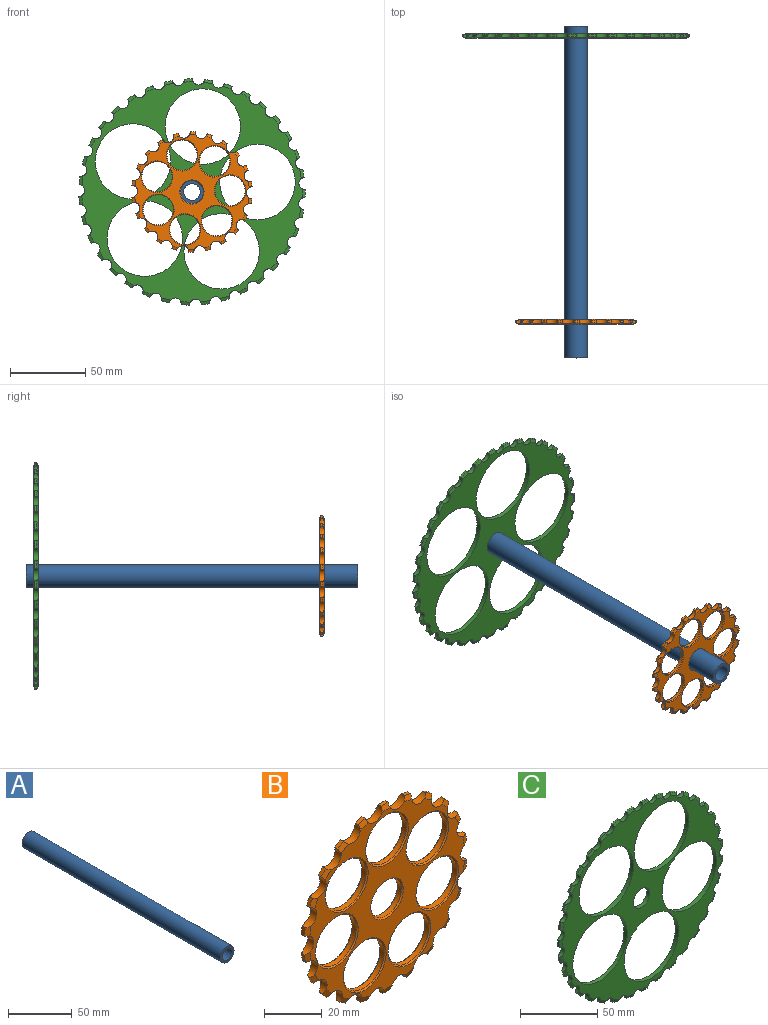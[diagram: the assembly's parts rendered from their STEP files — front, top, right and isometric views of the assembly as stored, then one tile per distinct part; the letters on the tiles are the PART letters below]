
ASSEMBLY  parts=3 mates=2
PART A: 4 faces, bbox 15x220x15 mm
  f0: cylinder r=5.5mm len=220mm, axis (0,1,0), area 7602.7mm2, adj f2,f3
  f1: cylinder r=7.5mm len=220mm, axis (0,1,0), area 10367.3mm2, adj f2,f3
  f2: plane 15x15mm, normal (0,-1,0), area 81.7mm2, adj f0,f1
  f3: plane 15x15mm, normal (0,1,0), area 81.7mm2, adj f0,f1
PART B: 114 faces, bbox 79.8x3x80 mm
  f0: cylinder r=4mm len=7.28mm, axis (0,1,0), area 33.4mm2, adj f1,f50,f52,f53,f61,f62,f83,f84
  f1: cylinder r=40mm len=3.13mm, axis (0,1,0), area 5.1mm2, adj f0,f2,f61,f83
  f2: cylinder r=4mm len=7.79mm, axis (0,1,0), area 33.4mm2, adj f1,f3,f52,f53,f60,f61,f82,f83
  f3: cylinder r=40mm len=3.39mm, axis (0,1,0), area 5.1mm2, adj f2,f4,f60,f82
  f4: cylinder r=4mm len=7.99mm, axis (0,1,0), area 33.4mm2, adj f3,f5,f52,f53,f59,f60,f81,f82
  f5: cylinder r=40mm len=3.38mm, axis (0,1,0), area 5.1mm2, adj f4,f6,f59,f81
  f6: cylinder r=4mm len=7.76mm, axis (0,1,0), area 33.4mm2, adj f5,f7,f52,f53,f58,f59,f80,f81
  f7: cylinder r=40mm len=3.09mm, axis (0,1,0), area 5.1mm2, adj f6,f8,f58,f80
  f8: cylinder r=4mm len=7.23mm, axis (0,1,0), area 33.4mm2, adj f7,f9,f52,f53,f57,f58,f79,f80
  f9: cylinder r=40mm len=2.56mm, axis (0,1,0), area 5.1mm2, adj f8,f10,f57,f79
  f10: cylinder r=4mm len=6.92mm, axis (0,1,0), area 33.4mm2, adj f9,f11,f52,f53,f56,f57,f78,f79
  f11: cylinder r=40mm len=2.9mm, axis (0,1,0), area 5.1mm2, adj f10,f12,f56,f78
  f12: cylinder r=4mm len=7.57mm, axis (0,1,0), area 33.4mm2, adj f11,f13,f52,f53,f55,f56,f77,f78
  f13: cylinder r=40mm len=3.29mm, axis (0,1,0), area 5.1mm2, adj f12,f14,f55,f77
  f14: cylinder r=4mm len=7.93mm, axis (0,1,0), area 33.4mm2, adj f13,f15,f52,f53,f54,f55,f76,f77
  f15: cylinder r=40mm len=3.42mm, axis (0,1,0), area 5.1mm2, adj f14,f16,f54,f76
  f16: cylinder r=4mm len=7.92mm, axis (0,1,0), area 33.4mm2, adj f15,f17,f52,f53,f54,f75,f76,f97
  f17: cylinder r=40mm len=3.27mm, axis (0,1,0), area 5.1mm2, adj f16,f18,f75,f97
  f18: cylinder r=4mm len=7.53mm, axis (0,1,0), area 33.4mm2, adj f17,f19,f52,f53,f74,f75,f96,f97
  f19: cylinder r=40mm len=2.86mm, axis (0,1,0), area 5.1mm2, adj f18,f20,f74,f96
  f20: cylinder r=4mm len=6.86mm, axis (0,1,0), area 33.4mm2, adj f19,f21,f52,f53,f73,f74,f95,f96
  f21: cylinder r=40mm len=2.61mm, axis (0,1,0), area 5.1mm2, adj f20,f22,f73,f95
  f22: cylinder r=4mm len=7.28mm, axis (0,1,0), area 33.4mm2, adj f21,f23,f52,f53,f72,f73,f94,f95
  f23: cylinder r=40mm len=3.13mm, axis (0,1,0), area 5.1mm2, adj f22,f24,f72,f94
  f24: cylinder r=4mm len=7.79mm, axis (0,1,0), area 33.4mm2, adj f23,f25,f52,f53,f71,f72,f93,f94
  f25: cylinder r=40mm len=3.39mm, axis (0,1,0), area 5.1mm2, adj f24,f26,f71,f93
  f26: cylinder r=4mm len=7.99mm, axis (0,1,0), area 33.4mm2, adj f25,f27,f52,f53,f70,f71,f92,f93
  f27: cylinder r=40mm len=3.38mm, axis (0,1,0), area 5.1mm2, adj f26,f28,f70,f92
  f28: cylinder r=4mm len=7.76mm, axis (0,1,0), area 33.4mm2, adj f27,f29,f52,f53,f69,f70,f91,f92
  f29: cylinder r=40mm len=3.09mm, axis (0,1,0), area 5.1mm2, adj f28,f30,f69,f91
  f30: cylinder r=4mm len=7.23mm, axis (0,1,0), area 33.4mm2, adj f29,f31,f52,f53,f68,f69,f90,f91
  f31: cylinder r=40mm len=2.56mm, axis (0,1,0), area 5.1mm2, adj f30,f32,f68,f90
  f32: cylinder r=4mm len=6.92mm, axis (0,1,0), area 33.4mm2, adj f31,f33,f52,f53,f67,f68,f89,f90
  f33: cylinder r=40mm len=2.9mm, axis (0,1,0), area 5.1mm2, adj f32,f34,f67,f89
  f34: cylinder r=4mm len=7.57mm, axis (0,1,0), area 33.4mm2, adj f33,f35,f52,f53,f66,f67,f88,f89
  f35: cylinder r=40mm len=3.29mm, axis (0,1,0), area 5.1mm2, adj f34,f36,f66,f88
  f36: cylinder r=4mm len=7.93mm, axis (0,1,0), area 33.4mm2, adj f35,f37,f52,f53,f65,f66,f87,f88
  f37: cylinder r=40mm len=3.42mm, axis (0,1,0), area 5.1mm2, adj f36,f38,f65,f87
  f38: cylinder r=4mm len=7.92mm, axis (0,1,0), area 33.4mm2, adj f37,f39,f52,f53,f64,f65,f86,f87
  f39: cylinder r=40mm len=3.27mm, axis (0,1,0), area 5.1mm2, adj f38,f40,f64,f86
  f40: cylinder r=4mm len=7.53mm, axis (0,1,0), area 33.4mm2, adj f39,f41,f52,f53,f63,f64,f85,f86
  f41: cylinder r=40mm len=2.86mm, axis (0,1,0), area 5.1mm2, adj f40,f42,f63,f85
  f42: cylinder r=4mm len=6.86mm, axis (0,1,0), area 33.4mm2, adj f41,f50,f52,f53,f62,f63,f84,f85
  f43: cylinder r=10mm len=20mm, axis (0,1,0), area 125.7mm2, adj f98,f105
  f44: cylinder r=10mm len=20mm, axis (0,1,0), area 125.7mm2, adj f99,f106
  f45: cylinder r=10mm len=20mm, axis (0,1,0), area 125.7mm2, adj f100,f107
  f46: cylinder r=10mm len=20mm, axis (0,1,0), area 125.7mm2, adj f101,f108
  f47: cylinder r=10mm len=20mm, axis (0,1,0), area 125.7mm2, adj f102,f109
  f48: cylinder r=10mm len=20mm, axis (0,1,0), area 125.7mm2, adj f103,f110
  f49: cylinder r=7.5mm len=15mm, axis (0,1,0), area 94.2mm2, adj f112,f113
  f50: cylinder r=40mm len=2.61mm, axis (0,1,0), area 5.1mm2, adj f0,f42,f62,f84
  f51: cylinder r=10mm len=20mm, axis (0,1,0), area 125.7mm2, adj f104,f111
  f52: plane 76x75.77mm, normal (0,-1,0), area 1702.4mm2, adj f0,f2,f4,f6,f8,f10,f12,f14
  f53: plane 76x75.77mm, normal (0,1,0), area 1702.4mm2, adj f0,f2,f4,f6,f8,f10,f12,f14
  f54: cone r=38mm half-angle=69.4deg, axis (0,1,0), area 7.6mm2, adj f14,f15,f16,f52
  f55: cone r=38mm half-angle=69.4deg, axis (0,1,0), area 7.6mm2, adj f12,f13,f14,f52
  f56: cone r=38mm half-angle=69.4deg, axis (0,1,0), area 7.6mm2, adj f10,f11,f12,f52
  f57: cone r=38mm half-angle=69.4deg, axis (0,1,0), area 7.6mm2, adj f8,f9,f10,f52
  f58: cone r=38mm half-angle=69.4deg, axis (0,1,0), area 7.6mm2, adj f6,f7,f8,f52
  f59: cone r=38mm half-angle=69.4deg, axis (0,1,0), area 7.6mm2, adj f4,f5,f6,f52
  f60: cone r=38mm half-angle=69.4deg, axis (0,1,0), area 7.6mm2, adj f2,f3,f4,f52
  f61: cone r=38mm half-angle=69.4deg, axis (0,1,0), area 7.6mm2, adj f0,f1,f2,f52
  f62: cone r=38mm half-angle=69.4deg, axis (0,1,0), area 7.6mm2, adj f0,f42,f50,f52
  f63: cone r=38mm half-angle=69.4deg, axis (0,1,0), area 7.6mm2, adj f40,f41,f42,f52
  f64: cone r=38mm half-angle=69.4deg, axis (0,1,0), area 7.6mm2, adj f38,f39,f40,f52
  f65: cone r=38mm half-angle=69.4deg, axis (0,1,0), area 7.6mm2, adj f36,f37,f38,f52
  f66: cone r=38mm half-angle=69.4deg, axis (0,1,0), area 7.6mm2, adj f34,f35,f36,f52
  f67: cone r=38mm half-angle=69.4deg, axis (0,1,0), area 7.6mm2, adj f32,f33,f34,f52
  f68: cone r=38mm half-angle=69.4deg, axis (0,1,0), area 7.6mm2, adj f30,f31,f32,f52
  f69: cone r=38mm half-angle=69.4deg, axis (0,1,0), area 7.6mm2, adj f28,f29,f30,f52
  f70: cone r=38mm half-angle=69.4deg, axis (0,1,0), area 7.6mm2, adj f26,f27,f28,f52
  f71: cone r=38mm half-angle=69.4deg, axis (0,1,0), area 7.6mm2, adj f24,f25,f26,f52
  f72: cone r=38mm half-angle=69.4deg, axis (0,1,0), area 7.6mm2, adj f22,f23,f24,f52
  f73: cone r=38mm half-angle=69.4deg, axis (0,1,0), area 7.6mm2, adj f20,f21,f22,f52
  f74: cone r=38mm half-angle=69.4deg, axis (0,1,0), area 7.6mm2, adj f18,f19,f20,f52
  f75: cone r=38mm half-angle=69.4deg, axis (0,1,0), area 7.6mm2, adj f16,f17,f18,f52
  f76: cone r=40mm half-angle=69.4deg, axis (0,-1,0), area 7.6mm2, adj f14,f15,f16,f53
  f77: cone r=40mm half-angle=69.4deg, axis (0,-1,0), area 7.6mm2, adj f12,f13,f14,f53
  f78: cone r=40mm half-angle=69.4deg, axis (0,-1,0), area 7.6mm2, adj f10,f11,f12,f53
  f79: cone r=40mm half-angle=69.4deg, axis (0,-1,0), area 7.6mm2, adj f8,f9,f10,f53
  f80: cone r=40mm half-angle=69.4deg, axis (0,-1,0), area 7.6mm2, adj f6,f7,f8,f53
  f81: cone r=40mm half-angle=69.4deg, axis (0,-1,0), area 7.6mm2, adj f4,f5,f6,f53
  f82: cone r=40mm half-angle=69.4deg, axis (0,-1,0), area 7.6mm2, adj f2,f3,f4,f53
  f83: cone r=40mm half-angle=69.4deg, axis (0,-1,0), area 7.6mm2, adj f0,f1,f2,f53
  f84: cone r=40mm half-angle=69.4deg, axis (0,-1,0), area 7.6mm2, adj f0,f42,f50,f53
  f85: cone r=40mm half-angle=69.4deg, axis (0,-1,0), area 7.6mm2, adj f40,f41,f42,f53
  f86: cone r=40mm half-angle=69.4deg, axis (0,-1,0), area 7.6mm2, adj f38,f39,f40,f53
  f87: cone r=40mm half-angle=69.4deg, axis (0,-1,0), area 7.6mm2, adj f36,f37,f38,f53
  f88: cone r=40mm half-angle=69.4deg, axis (0,-1,0), area 7.6mm2, adj f34,f35,f36,f53
  f89: cone r=40mm half-angle=69.4deg, axis (0,-1,0), area 7.6mm2, adj f32,f33,f34,f53
  f90: cone r=40mm half-angle=69.4deg, axis (0,-1,0), area 7.6mm2, adj f30,f31,f32,f53
  f91: cone r=40mm half-angle=69.4deg, axis (0,-1,0), area 7.6mm2, adj f28,f29,f30,f53
  f92: cone r=40mm half-angle=69.4deg, axis (0,-1,0), area 7.6mm2, adj f26,f27,f28,f53
  f93: cone r=40mm half-angle=69.4deg, axis (0,-1,0), area 7.6mm2, adj f24,f25,f26,f53
  f94: cone r=40mm half-angle=69.4deg, axis (0,-1,0), area 7.6mm2, adj f22,f23,f24,f53
  f95: cone r=40mm half-angle=69.4deg, axis (0,-1,0), area 7.6mm2, adj f20,f21,f22,f53
  f96: cone r=40mm half-angle=69.4deg, axis (0,-1,0), area 7.6mm2, adj f18,f19,f20,f53
  f97: cone r=40mm half-angle=69.4deg, axis (0,-1,0), area 7.6mm2, adj f16,f17,f18,f53
  f98: cone r=10.5mm half-angle=45deg, axis (0,1,0), area 45.5mm2, adj f43,f53
  f99: cone r=10.5mm half-angle=45deg, axis (0,1,0), area 45.5mm2, adj f44,f53
  f100: cone r=10.5mm half-angle=45deg, axis (0,1,0), area 45.5mm2, adj f45,f53
  f101: cone r=10.5mm half-angle=45deg, axis (0,1,0), area 45.5mm2, adj f46,f53
  f102: cone r=10.5mm half-angle=45deg, axis (0,1,0), area 45.5mm2, adj f47,f53
  f103: cone r=10.5mm half-angle=45deg, axis (0,1,0), area 45.5mm2, adj f48,f53
  f104: cone r=10.5mm half-angle=45deg, axis (0,1,0), area 45.5mm2, adj f51,f53
  f105: cone r=10mm half-angle=45deg, axis (0,-1,0), area 45.5mm2, adj f43,f52
  f106: cone r=10mm half-angle=45deg, axis (0,-1,0), area 45.5mm2, adj f44,f52
  f107: cone r=10mm half-angle=45deg, axis (0,-1,0), area 45.5mm2, adj f45,f52
  f108: cone r=10mm half-angle=45deg, axis (0,-1,0), area 45.5mm2, adj f46,f52
  f109: cone r=10mm half-angle=45deg, axis (0,-1,0), area 45.5mm2, adj f47,f52
  f110: cone r=10mm half-angle=45deg, axis (0,-1,0), area 45.5mm2, adj f48,f52
  f111: cone r=10mm half-angle=45deg, axis (0,-1,0), area 45.5mm2, adj f51,f52
  f112: cone r=8mm half-angle=45deg, axis (0,1,0), area 34.4mm2, adj f49,f53
  f113: cone r=7.5mm half-angle=45deg, axis (0,-1,0), area 34.4mm2, adj f49,f52
PART C: 148 faces, bbox 149.9x3x150 mm
  f0: cylinder r=75mm len=5.21mm, axis (0,1,0), area 8.2mm2, adj f35,f68,f145,f146
  f1: cylinder r=75mm len=5.42mm, axis (0,1,0), area 8.2mm2, adj f36,f70,f144,f145
  f2: cylinder r=75mm len=5.46mm, axis (0,1,0), area 8.2mm2, adj f37,f71,f143,f144
  f3: cylinder r=75mm len=5.32mm, axis (0,1,0), area 8.2mm2, adj f38,f73,f142,f143
  f4: cylinder r=75mm len=5.01mm, axis (0,1,0), area 8.2mm2, adj f39,f72,f141,f142
  f5: cylinder r=75mm len=4.54mm, axis (0,1,0), area 8.2mm2, adj f40,f74,f140,f141
  f6: cylinder r=75mm len=3.93mm, axis (0,1,0), area 8.2mm2, adj f41,f75,f139,f140
  f7: cylinder r=75mm len=4.44mm, axis (0,1,0), area 8.2mm2, adj f42,f79,f138,f139
  f8: cylinder r=75mm len=4.94mm, axis (0,1,0), area 8.2mm2, adj f43,f76,f137,f138
  f9: cylinder r=75mm len=5.28mm, axis (0,1,0), area 8.2mm2, adj f44,f77,f136,f137
  f10: cylinder r=75mm len=5.44mm, axis (0,1,0), area 8.2mm2, adj f45,f78,f135,f136
  f11: cylinder r=75mm len=5.44mm, axis (0,1,0), area 8.2mm2, adj f46,f80,f134,f135
  f12: cylinder r=75mm len=5.26mm, axis (0,1,0), area 8.2mm2, adj f47,f82,f133,f134
  f13: cylinder r=75mm len=4.91mm, axis (0,1,0), area 8.2mm2, adj f48,f81,f132,f133
  f14: cylinder r=75mm len=4.4mm, axis (0,1,0), area 8.2mm2, adj f49,f83,f131,f132
  f15: cylinder r=75mm len=3.97mm, axis (0,1,0), area 8.2mm2, adj f50,f84,f130,f131
  f16: cylinder r=75mm len=4.58mm, axis (0,1,0), area 8.2mm2, adj f52,f87,f129,f130
  f17: cylinder r=75mm len=5.04mm, axis (0,1,0), area 8.2mm2, adj f51,f85,f128,f129
  f18: cylinder r=75mm len=5.33mm, axis (0,1,0), area 8.2mm2, adj f53,f86,f127,f128
  f19: cylinder r=75mm len=5.46mm, axis (0,1,0), area 8.2mm2, adj f54,f88,f126,f127
  f20: cylinder r=75mm len=5.41mm, axis (0,1,0), area 8.2mm2, adj f55,f89,f125,f126
  f21: cylinder r=75mm len=5.19mm, axis (0,1,0), area 8.2mm2, adj f56,f91,f124,f125
  f22: cylinder r=75mm len=4.8mm, axis (0,1,0), area 8.2mm2, adj f57,f90,f123,f124
  f23: cylinder r=75mm len=4.25mm, axis (0,1,0), area 8.2mm2, adj f58,f92,f122,f123
  f24: cylinder r=75mm len=4.14mm, axis (0,1,0), area 8.2mm2, adj f59,f93,f121,f122
  f25: cylinder r=75mm len=4.71mm, axis (0,1,0), area 8.2mm2, adj f60,f96,f120,f121
  f26: cylinder r=75mm len=5.13mm, axis (0,1,0), area 8.2mm2, adj f62,f94,f119,f120
  f27: cylinder r=75mm len=5.38mm, axis (0,1,0), area 8.2mm2, adj f61,f95,f118,f119
  f28: cylinder r=75mm len=5.46mm, axis (0,1,0), area 8.2mm2, adj f63,f97,f117,f118
  f29: cylinder r=75mm len=5.37mm, axis (0,1,0), area 8.2mm2, adj f64,f98,f116,f117
  f30: cylinder r=75mm len=5.1mm, axis (0,1,0), area 8.2mm2, adj f65,f101,f115,f116
  f31: cylinder r=75mm len=4.67mm, axis (0,1,0), area 8.2mm2, adj f67,f99,f113,f115
  f32: cylinder r=75mm len=4.29mm, axis (0,1,0), area 8.2mm2, adj f110,f111,f112,f114
  f33: cylinder r=75mm len=4.09mm, axis (0,1,0), area 8.2mm2, adj f66,f100,f113,f114
  f34: cone r=73mm half-angle=69.4deg, axis (0,1,0), area 12.2mm2, adj f107,f108,f112,f146
  f35: cone r=73mm half-angle=69.4deg, axis (0,1,0), area 12.2mm2, adj f0,f108,f145,f146
  f36: cone r=73mm half-angle=69.4deg, axis (0,1,0), area 12.2mm2, adj f1,f108,f144,f145
  f37: cone r=73mm half-angle=69.4deg, axis (0,1,0), area 12.2mm2, adj f2,f108,f143,f144
  f38: cone r=73mm half-angle=69.4deg, axis (0,1,0), area 12.2mm2, adj f3,f108,f142,f143
  f39: cone r=73mm half-angle=69.4deg, axis (0,1,0), area 12.2mm2, adj f4,f108,f141,f142
  f40: cone r=73mm half-angle=69.4deg, axis (0,1,0), area 12.2mm2, adj f5,f108,f140,f141
  f41: cone r=73mm half-angle=69.4deg, axis (0,1,0), area 12.2mm2, adj f6,f108,f139,f140
  f42: cone r=73mm half-angle=69.4deg, axis (0,1,0), area 12.2mm2, adj f7,f108,f138,f139
  f43: cone r=73mm half-angle=69.4deg, axis (0,1,0), area 12.2mm2, adj f8,f108,f137,f138
  f44: cone r=73mm half-angle=69.4deg, axis (0,1,0), area 12.2mm2, adj f9,f108,f136,f137
  f45: cone r=73mm half-angle=69.4deg, axis (0,1,0), area 12.2mm2, adj f10,f108,f135,f136
  f46: cone r=73mm half-angle=69.4deg, axis (0,1,0), area 12.2mm2, adj f11,f108,f134,f135
  f47: cone r=73mm half-angle=69.4deg, axis (0,1,0), area 12.2mm2, adj f12,f108,f133,f134
  f48: cone r=73mm half-angle=69.4deg, axis (0,1,0), area 12.2mm2, adj f13,f108,f132,f133
  f49: cone r=73mm half-angle=69.4deg, axis (0,1,0), area 12.2mm2, adj f14,f108,f131,f132
  f50: cone r=73mm half-angle=69.4deg, axis (0,1,0), area 12.2mm2, adj f15,f108,f130,f131
  f51: cone r=73mm half-angle=69.4deg, axis (0,1,0), area 12.2mm2, adj f17,f108,f128,f129
  f52: cone r=73mm half-angle=69.4deg, axis (0,1,0), area 12.2mm2, adj f16,f108,f129,f130
  f53: cone r=73mm half-angle=69.4deg, axis (0,1,0), area 12.2mm2, adj f18,f108,f127,f128
  f54: cone r=73mm half-angle=69.4deg, axis (0,1,0), area 12.2mm2, adj f19,f108,f126,f127
  f55: cone r=73mm half-angle=69.4deg, axis (0,1,0), area 12.2mm2, adj f20,f108,f125,f126
  f56: cone r=73mm half-angle=69.4deg, axis (0,1,0), area 12.2mm2, adj f21,f108,f124,f125
  f57: cone r=73mm half-angle=69.4deg, axis (0,1,0), area 12.2mm2, adj f22,f108,f123,f124
  f58: cone r=73mm half-angle=69.4deg, axis (0,1,0), area 12.2mm2, adj f23,f108,f122,f123
  f59: cone r=73mm half-angle=69.4deg, axis (0,1,0), area 12.2mm2, adj f24,f108,f121,f122
  f60: cone r=73mm half-angle=69.4deg, axis (0,1,0), area 12.2mm2, adj f25,f108,f120,f121
  f61: cone r=73mm half-angle=69.4deg, axis (0,1,0), area 12.2mm2, adj f27,f108,f118,f119
  f62: cone r=73mm half-angle=69.4deg, axis (0,1,0), area 12.2mm2, adj f26,f108,f119,f120
  f63: cone r=73mm half-angle=69.4deg, axis (0,1,0), area 12.2mm2, adj f28,f108,f117,f118
  f64: cone r=73mm half-angle=69.4deg, axis (0,1,0), area 12.2mm2, adj f29,f108,f116,f117
  f65: cone r=73mm half-angle=69.4deg, axis (0,1,0), area 12.2mm2, adj f30,f108,f115,f116
  f66: cone r=73mm half-angle=69.4deg, axis (0,1,0), area 12.2mm2, adj f33,f108,f113,f114
  f67: cone r=73mm half-angle=69.4deg, axis (0,1,0), area 12.2mm2, adj f31,f108,f113,f115
  f68: cone r=75mm half-angle=69.4deg, axis (0,-1,0), area 12.2mm2, adj f0,f109,f145,f146
  f69: cone r=75mm half-angle=69.4deg, axis (0,-1,0), area 12.2mm2, adj f107,f109,f112,f146
  f70: cone r=75mm half-angle=69.4deg, axis (0,-1,0), area 12.2mm2, adj f1,f109,f144,f145
  f71: cone r=75mm half-angle=69.4deg, axis (0,-1,0), area 12.2mm2, adj f2,f109,f143,f144
  f72: cone r=75mm half-angle=69.4deg, axis (0,-1,0), area 12.2mm2, adj f4,f109,f141,f142
  f73: cone r=75mm half-angle=69.4deg, axis (0,-1,0), area 12.2mm2, adj f3,f109,f142,f143
  f74: cone r=75mm half-angle=69.4deg, axis (0,-1,0), area 12.2mm2, adj f5,f109,f140,f141
  f75: cone r=75mm half-angle=69.4deg, axis (0,-1,0), area 12.2mm2, adj f6,f109,f139,f140
  f76: cone r=75mm half-angle=69.4deg, axis (0,-1,0), area 12.2mm2, adj f8,f109,f137,f138
  f77: cone r=75mm half-angle=69.4deg, axis (0,-1,0), area 12.2mm2, adj f9,f109,f136,f137
  f78: cone r=75mm half-angle=69.4deg, axis (0,-1,0), area 12.2mm2, adj f10,f109,f135,f136
  f79: cone r=75mm half-angle=69.4deg, axis (0,-1,0), area 12.2mm2, adj f7,f109,f138,f139
  f80: cone r=75mm half-angle=69.4deg, axis (0,-1,0), area 12.2mm2, adj f11,f109,f134,f135
  f81: cone r=75mm half-angle=69.4deg, axis (0,-1,0), area 12.2mm2, adj f13,f109,f132,f133
  f82: cone r=75mm half-angle=69.4deg, axis (0,-1,0), area 12.2mm2, adj f12,f109,f133,f134
  f83: cone r=75mm half-angle=69.4deg, axis (0,-1,0), area 12.2mm2, adj f14,f109,f131,f132
  f84: cone r=75mm half-angle=69.4deg, axis (0,-1,0), area 12.2mm2, adj f15,f109,f130,f131
  f85: cone r=75mm half-angle=69.4deg, axis (0,-1,0), area 12.2mm2, adj f17,f109,f128,f129
  f86: cone r=75mm half-angle=69.4deg, axis (0,-1,0), area 12.2mm2, adj f18,f109,f127,f128
  f87: cone r=75mm half-angle=69.4deg, axis (0,-1,0), area 12.2mm2, adj f16,f109,f129,f130
  f88: cone r=75mm half-angle=69.4deg, axis (0,-1,0), area 12.2mm2, adj f19,f109,f126,f127
  f89: cone r=75mm half-angle=69.4deg, axis (0,-1,0), area 12.2mm2, adj f20,f109,f125,f126
  f90: cone r=75mm half-angle=69.4deg, axis (0,-1,0), area 12.2mm2, adj f22,f109,f123,f124
  f91: cone r=75mm half-angle=69.4deg, axis (0,-1,0), area 12.2mm2, adj f21,f109,f124,f125
  f92: cone r=75mm half-angle=69.4deg, axis (0,-1,0), area 12.2mm2, adj f23,f109,f122,f123
  f93: cone r=75mm half-angle=69.4deg, axis (0,-1,0), area 12.2mm2, adj f24,f109,f121,f122
  f94: cone r=75mm half-angle=69.4deg, axis (0,-1,0), area 12.2mm2, adj f26,f109,f119,f120
  f95: cone r=75mm half-angle=69.4deg, axis (0,-1,0), area 12.2mm2, adj f27,f109,f118,f119
  f96: cone r=75mm half-angle=69.4deg, axis (0,-1,0), area 12.2mm2, adj f25,f109,f120,f121
  f97: cone r=75mm half-angle=69.4deg, axis (0,-1,0), area 12.2mm2, adj f28,f109,f117,f118
  f98: cone r=75mm half-angle=69.4deg, axis (0,-1,0), area 12.2mm2, adj f29,f109,f116,f117
  f99: cone r=75mm half-angle=69.4deg, axis (0,-1,0), area 12.2mm2, adj f31,f109,f113,f115
  f100: cone r=75mm half-angle=69.4deg, axis (0,-1,0), area 12.2mm2, adj f33,f109,f113,f114
  f101: cone r=75mm half-angle=69.4deg, axis (0,-1,0), area 12.2mm2, adj f30,f109,f115,f116
  f102: cylinder r=25mm len=50mm, axis (0,1,0), area 471.2mm2, adj f108,f109
  f103: cylinder r=25mm len=50mm, axis (0,1,0), area 471.2mm2, adj f108,f109
  f104: cylinder r=25mm len=50mm, axis (0,1,0), area 471.2mm2, adj f108,f109
  f105: cylinder r=25mm len=50mm, axis (0,1,0), area 471.2mm2, adj f108,f109
  f106: cylinder r=25mm len=50mm, axis (0,1,0), area 471.2mm2, adj f108,f109
  f107: cylinder r=75mm len=4.83mm, axis (0,1,0), area 8.2mm2, adj f34,f69,f112,f146
  f108: plane 146x145.94mm, normal (0,-1,0), area 6417.7mm2, adj f34,f35,f36,f37,f38,f39,f40,f41
  f109: plane 146x145.94mm, normal (0,1,0), area 6417.7mm2, adj f68,f69,f70,f71,f72,f73,f74,f75
  f110: cone r=73mm half-angle=69.4deg, axis (0,1,0), area 12.2mm2, adj f32,f108,f112,f114
  f111: cone r=75mm half-angle=69.4deg, axis (0,-1,0), area 12.2mm2, adj f32,f109,f112,f114
  f112: cylinder r=4mm len=7.27mm, axis (0,-1,0), area 33.7mm2, adj f32,f34,f69,f107,f108,f109,f110,f111
  f113: cylinder r=4mm len=7.14mm, axis (0,-1,0), area 33.7mm2, adj f31,f33,f66,f67,f99,f100,f108,f109
  f114: cylinder r=4mm len=6.81mm, axis (0,-1,0), area 33.7mm2, adj f32,f33,f66,f100,f108,f109,f110,f111
  f115: cylinder r=4mm len=7.53mm, axis (0,-1,0), area 33.7mm2, adj f30,f31,f65,f67,f99,f101,f108,f109
  f116: cylinder r=4mm len=7.81mm, axis (0,-1,0), area 33.7mm2, adj f29,f30,f64,f65,f98,f101,f108,f109
  f117: cylinder r=4mm len=7.97mm, axis (0,-1,0), area 33.7mm2, adj f28,f29,f63,f64,f97,f98,f108,f109
  f118: cylinder r=4mm len=7.97mm, axis (0,-1,0), area 33.7mm2, adj f27,f28,f61,f63,f95,f97,f108,f109
  f119: cylinder r=4mm len=7.82mm, axis (0,-1,0), area 33.7mm2, adj f26,f27,f61,f62,f94,f95,f108,f109
  f120: cylinder r=4mm len=7.55mm, axis (0,-1,0), area 33.7mm2, adj f25,f26,f60,f62,f94,f96,f108,f109
  f121: cylinder r=4mm len=7.17mm, axis (0,-1,0), area 33.7mm2, adj f24,f25,f59,f60,f93,f96,f108,f109
  f122: cylinder r=4mm len=6.78mm, axis (0,-1,0), area 33.7mm2, adj f23,f24,f58,f59,f92,f93,f108,f109
  f123: cylinder r=4mm len=7.25mm, axis (0,-1,0), area 33.7mm2, adj f22,f23,f57,f58,f90,f92,f108,f109
  f124: cylinder r=4mm len=7.61mm, axis (0,-1,0), area 33.7mm2, adj f21,f22,f56,f57,f90,f91,f108,f109
  f125: cylinder r=4mm len=7.86mm, axis (0,-1,0), area 33.7mm2, adj f20,f21,f55,f56,f89,f91,f108,f109
  f126: cylinder r=4mm len=7.99mm, axis (0,-1,0), area 33.7mm2, adj f19,f20,f54,f55,f88,f89,f108,f109
  f127: cylinder r=4mm len=7.95mm, axis (0,-1,0), area 33.7mm2, adj f18,f19,f53,f54,f86,f88,f108,f109
  f128: cylinder r=4mm len=7.77mm, axis (0,-1,0), area 33.7mm2, adj f17,f18,f51,f53,f85,f86,f108,f109
  f129: cylinder r=4mm len=7.47mm, axis (0,-1,0), area 33.7mm2, adj f16,f17,f51,f52,f85,f87,f108,f109
  f130: cylinder r=4mm len=7.05mm, axis (0,-1,0), area 33.7mm2, adj f15,f16,f50,f52,f84,f87,f108,f109
  f131: cylinder r=4mm len=6.9mm, axis (0,-1,0), area 33.7mm2, adj f14,f15,f49,f50,f83,f84,f108,f109
  f132: cylinder r=4mm len=7.35mm, axis (0,-1,0), area 33.7mm2, adj f13,f14,f48,f49,f81,f83,f108,f109
  f133: cylinder r=4mm len=7.68mm, axis (0,-1,0), area 33.7mm2, adj f12,f13,f47,f48,f81,f82,f108,f109
  f134: cylinder r=4mm len=7.9mm, axis (0,-1,0), area 33.7mm2, adj f11,f12,f46,f47,f80,f82,f108,f109
  f135: cylinder r=4mm len=8mm, axis (0,-1,0), area 33.7mm2, adj f10,f11,f45,f46,f78,f80,f108,f109
  f136: cylinder r=4mm len=7.91mm, axis (0,-1,0), area 33.7mm2, adj f9,f10,f44,f45,f77,f78,f108,f109
  f137: cylinder r=4mm len=7.7mm, axis (0,-1,0), area 33.7mm2, adj f8,f9,f43,f44,f76,f77,f108,f109
  f138: cylinder r=4mm len=7.37mm, axis (0,-1,0), area 33.7mm2, adj f7,f8,f42,f43,f76,f79,f108,f109
  f139: cylinder r=4mm len=6.93mm, axis (0,-1,0), area 33.7mm2, adj f6,f7,f41,f42,f75,f79,f108,f109
  f140: cylinder r=4mm len=7.02mm, axis (0,-1,0), area 33.7mm2, adj f5,f6,f40,f41,f74,f75,f108,f109
  f141: cylinder r=4mm len=7.44mm, axis (0,-1,0), area 33.7mm2, adj f4,f5,f39,f40,f72,f74,f108,f109
  f142: cylinder r=4mm len=7.75mm, axis (0,-1,0), area 33.7mm2, adj f3,f4,f38,f39,f72,f73,f108,f109
  f143: cylinder r=4mm len=7.94mm, axis (0,-1,0), area 33.7mm2, adj f2,f3,f37,f38,f71,f73,f108,f109
  f144: cylinder r=4mm len=7.99mm, axis (0,-1,0), area 33.7mm2, adj f1,f2,f36,f37,f70,f71,f108,f109
  f145: cylinder r=4mm len=7.87mm, axis (0,-1,0), area 33.7mm2, adj f0,f1,f35,f36,f68,f70,f108,f109
  f146: cylinder r=4mm len=7.63mm, axis (0,-1,0), area 33.7mm2, adj f0,f34,f35,f68,f69,f107,f108,f109
  f147: cylinder r=7.5mm len=15mm, axis (0,-1,0), area 141.4mm2, adj f108,f109
PLACE A rot(axis=(0,-1,0),15deg) t=(-10.25,14.5,-3.43)mm
PLACE B rot(axis=(0,-1,0),15deg) t=(-10.25,-180,-3.43)mm
PLACE C rot(axis=(0,-1,0),15deg) t=(-10.25,9.5,-3.43)mm
MATE fastened B.f49 <-> A.f1  axis (0,-1,0) through (-10.25,-180.5,-3.43)mm
MATE fastened C.f0 <-> A.f1  axis (0,1,0) through (-10.25,9.5,-3.43)mm
